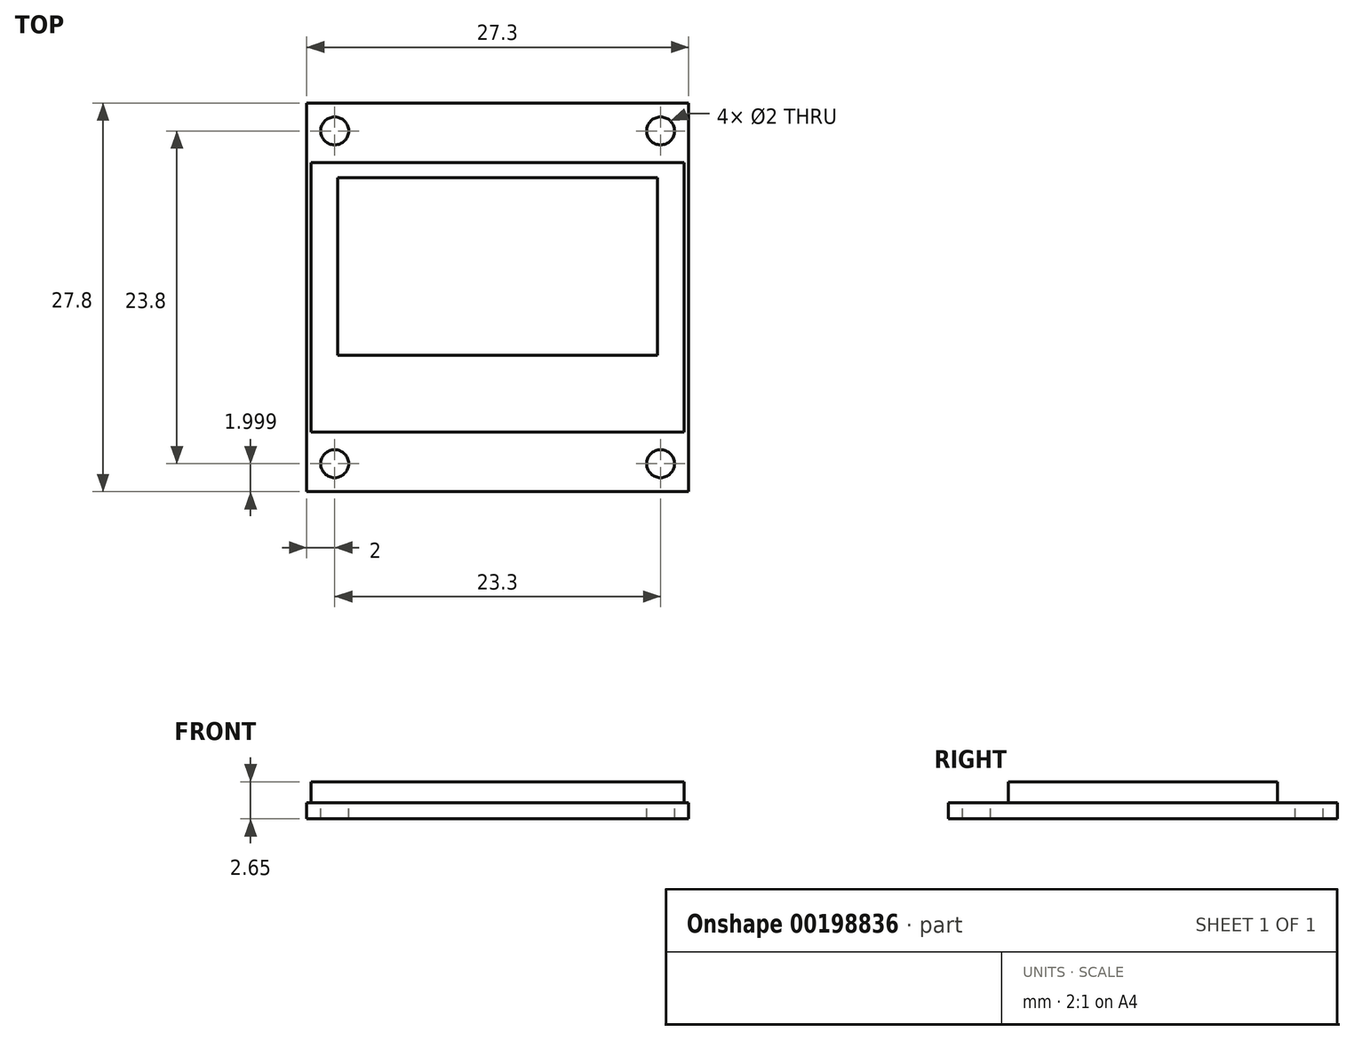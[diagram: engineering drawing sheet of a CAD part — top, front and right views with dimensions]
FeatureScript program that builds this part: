
annotation { "Feature Type Name" : "Feature", "Feature Type Description" : "" }
export const myFeature = defineFeature(function(context is Context, id is Id, definition is map)
    precondition{}
    {
        {
            var Q0;
            Q0=qCreatedBy(makeId("Top.planeOp"),FACE);
            var sketch = newSketch(context, id + "F0", { "sketchPlane" : qUnion([Q0])});
            skLineSegment(sketch, "E0.bottom", {"start": v(11.43, -6.35) * mm, "end": v(-11.43, -6.35) * mm});
            skLineSegment(sketch, "E0.top", {"start": v(11.43, 6.35) * mm, "end": v(-11.43, 6.35) * mm});
            skLineSegment(sketch, "E0.left", {"start": v(11.43, -6.35) * mm, "end": v(11.43, 6.35) * mm});
            skLineSegment(sketch, "E0.right", {"start": v(-11.43, -6.35) * mm, "end": v(-11.43, 6.35) * mm});
            skPoint(sketch, "E0.middle", {"position": v(0, 0) * mm});
            skLineSegment(sketch, "E1.bottom", {"start": v(13.65, 11.7) * mm, "end": v(-13.65, 11.7) * mm});
            skLineSegment(sketch, "E1.top", {"start": v(13.65, -16.1) * mm, "end": v(-13.65, -16.1) * mm});
            skLineSegment(sketch, "E1.left", {"start": v(13.65, 11.7) * mm, "end": v(13.65, -16.1) * mm});
            skLineSegment(sketch, "E1.right", {"start": v(-13.65, 11.7) * mm, "end": v(-13.65, -16.1) * mm});
            skPoint(sketch, "E1.middle", {"position": v(0, -2.2) * mm});
            skLineSegment(sketch, "E2.bottom", {"start": v(-13.34, 7.44) * mm, "end": v(13.34, 7.44) * mm});
            skLineSegment(sketch, "E2.top", {"start": v(-13.34, -11.82) * mm, "end": v(13.34, -11.82) * mm});
            skLineSegment(sketch, "E2.left", {"start": v(-13.34, 7.44) * mm, "end": v(-13.34, -11.82) * mm});
            skLineSegment(sketch, "E2.right", {"start": v(13.33, 7.44) * mm, "end": v(13.33, -11.82) * mm});
            skSolve(sketch);
        }
        {
            var Q0;
            Q0=makeQuery(id+"F0.imprint","IMPRINT",FACE,{"disambiguationData":[TD([[makeQuery(id+"F0.imprint","IMPRINT",EDGE,{"derivedFrom":sQuery(id+"F0.wireOp",EDGE,"E1.bottom")}),1.0]])]});
            var Q1;
            Q1=makeQuery(id+"F0.imprint","IMPRINT",FACE,{"disambiguationData":[TD([[makeQuery(id+"F0.imprint","IMPRINT",EDGE,{"derivedFrom":sQuery(id+"F0.wireOp",EDGE,"E0.bottom")}),1.0]])]});
            var Q2;
            Q2=makeQuery(id+"F0.imprint","IMPRINT",FACE,{"disambiguationData":[TD([[makeQuery(id+"F0.imprint","IMPRINT",EDGE,{"derivedFrom":sQuery(id+"F0.wireOp",EDGE,"E0.bottom")}),-1.0]])]});
            extrude(context, id + "F1", {"entities" : qUnion([Q0, Q1, Q2]), "oppositeDirection" : true, "depth" : 1.14 * mm});
        }
        {
            var Q0;
            Q0=makeQuery(id+"F0.imprint","IMPRINT",FACE,{"disambiguationData":[TD([[makeQuery(id+"F0.imprint","IMPRINT",EDGE,{"derivedFrom":sQuery(id+"F0.wireOp",EDGE,"E0.bottom")}),1.0]])]});
            var Q1;
            Q1=makeQuery(id+"F0.imprint","IMPRINT",FACE,{"disambiguationData":[TD([[makeQuery(id+"F0.imprint","IMPRINT",EDGE,{"derivedFrom":sQuery(id+"F0.wireOp",EDGE,"E0.bottom")}),-1.0]])]});
            extrude(context, id + "F2", {"entities" : qUnion([Q0, Q1]), "operationType" : NewBodyOperationType.ADD, "depth" : 1.5 * mm});
        }
        {
            var Q0;
            Q0=makeQuery(id+"F0.imprint","IMPRINT",FACE,{"disambiguationData":[TD([[makeQuery(id+"F0.imprint","IMPRINT",EDGE,{"derivedFrom":sQuery(id+"F0.wireOp",EDGE,"E0.bottom")}),-1.0]])]});
            extrude(context, id + "F3", {"entities" : qUnion([Q0]), "operationType" : NewBodyOperationType.ADD, "depth" : 1.51 * mm});
        }
        {
            var Q0;
            Q0=makeQuery(id+"F0.imprint","IMPRINT",FACE,{"disambiguationData":[TD([[makeQuery(id+"F0.imprint","IMPRINT",EDGE,{"derivedFrom":sQuery(id+"F0.wireOp",EDGE,"E1.bottom")}),1.0]])]});
            var sketch = newSketch(context, id + "F4", { "sketchPlane" : qUnion([Q0])});
            skPoint(sketch, "E3", {"position": v(-11.65, 9.7) * mm});
            skPoint(sketch, "E4", {"position": v(11.65, 9.7) * mm});
            skPoint(sketch, "E5", {"position": v(11.65, -14.1) * mm});
            skPoint(sketch, "E6", {"position": v(-11.65, -14.1) * mm});
            skSolve(sketch);
        }
        {
            var Q0;
            Q0=sQuery(id+"F4.wireOp",VERTEX,"E3");
            var Q1;
            Q1=sQuery(id+"F4.wireOp",VERTEX,"E4");
            var Q2;
            Q2=sQuery(id+"F4.wireOp",VERTEX,"E5");
            var Q3;
            Q3=sQuery(id+"F4.wireOp",VERTEX,"E6");
            var Q4;
            Q4=makeQuery(id+"F1.opExtrude","SWEPT_BODY",BODY,{"disambiguationData":[OSD([sQuery(id+"F0.wireOp",EDGE,"E1.bottom"),sQuery(id+"F0.wireOp",EDGE,"E1.top"),sQuery(id+"F0.wireOp",EDGE,"E1.left"),sQuery(id+"F0.wireOp",EDGE,"E1.right")])]});
            hole(context, id + "F5", {"style" : HoleStyle.SIMPLE, "endStyle" : HoleEndStyle.THROUGH, "holeDiameter" : 2 * mm, "locations" : qUnion([Q0, Q1, Q2, Q3]), "scope" : qUnion([Q4]), "isTappedThrough" : true});
        }
    });
